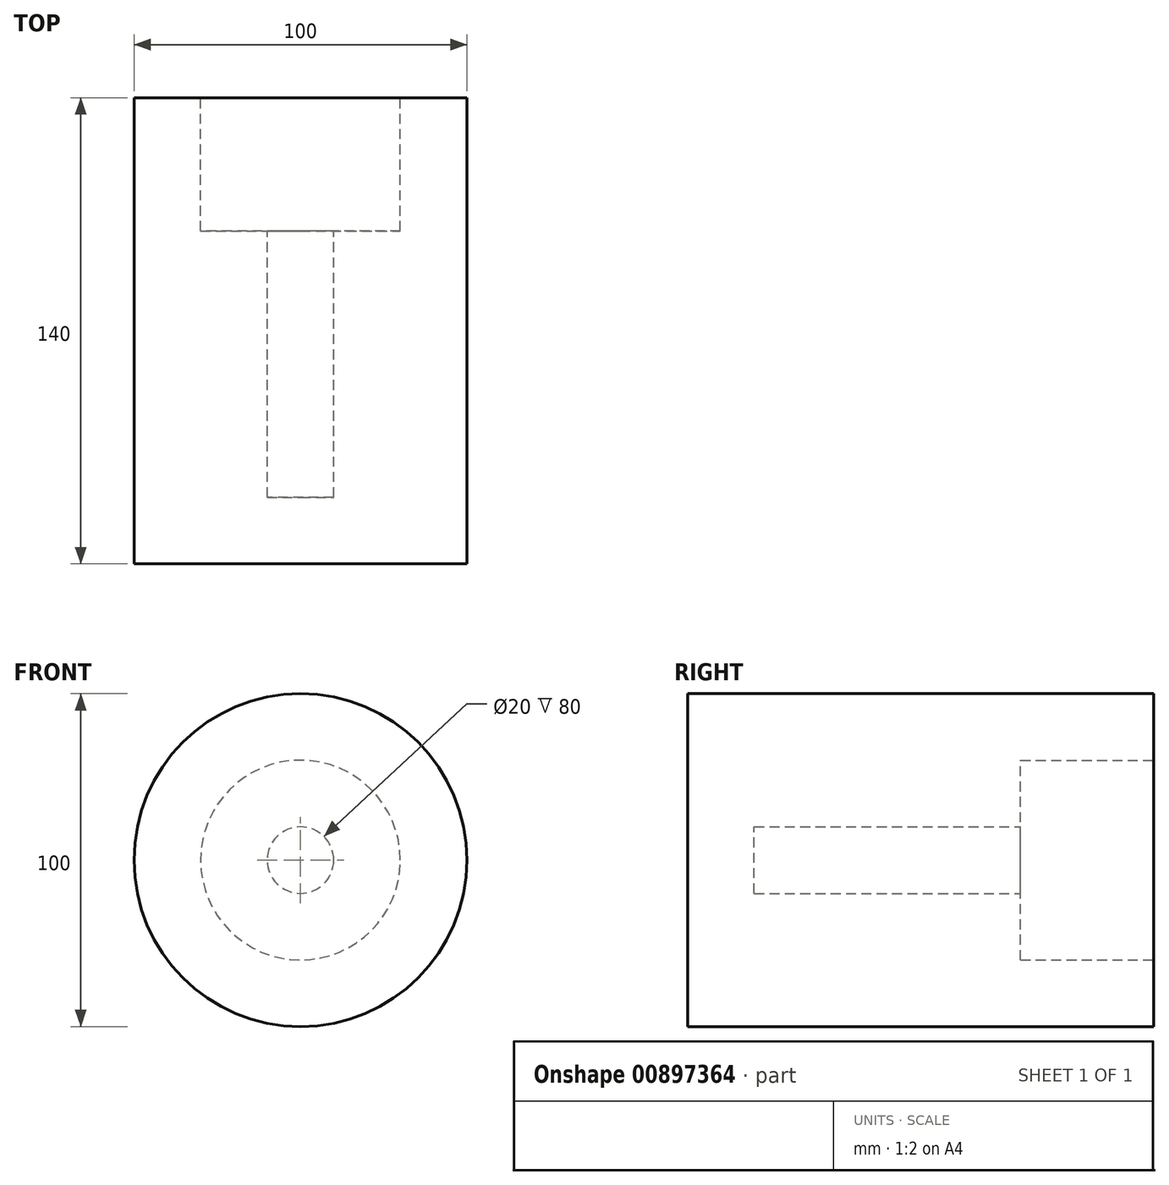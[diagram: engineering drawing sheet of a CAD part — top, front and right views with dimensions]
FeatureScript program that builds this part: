
annotation { "Feature Type Name" : "Feature", "Feature Type Description" : "" }
export const myFeature = defineFeature(function(context is Context, id is Id, definition is map)
    precondition{}
    {
        {
            var Q0;
            Q0=qCreatedBy(makeId("Front.planeOp"),FACE);
            var sketch = newSketch(context, id + "F0", { "sketchPlane" : qUnion([Q0])});
            skCircle(sketch, "E0", {"center": v(0, 0) * mm, "radius": 50 * mm});
            skSolve(sketch);
        }
        {
            var Q0;
            Q0=makeQuery(id+"F0.imprint","IMPRINT",FACE,{"disambiguationData":[TD([[makeQuery(id+"F0.imprint","IMPRINT",EDGE,{"derivedFrom":sQuery(id+"F0.wireOp",EDGE,"E0")}),1.0]])]});
            extrude(context, id + "F1", {"entities" : qUnion([Q0]), "depth" : 140 * mm, "offsetDistance" : 25.4 * mm});
        }
        {
            var Q0;
            Q0=qCreatedBy(makeId("Front.planeOp"),FACE);
            var sketch = newSketch(context, id + "F2", { "sketchPlane" : qUnion([Q0])});
            skCircle(sketch, "E1", {"center": v(0, 0) * mm, "radius": 30 * mm});
            skSolve(sketch);
        }
        {
            var Q0;
            Q0 = qSketchRegion(id + "F2", true);
            extrude(context, id + "F3", {"entities" : qUnion([Q0]), "operationType" : NewBodyOperationType.REMOVE, "depth" : 40 * mm, "offsetDistance" : 25.4 * mm});
        }
        {
            var Q0;
            Q0=qCreatedBy(makeId("Front.planeOp"),FACE);
            var sketch = newSketch(context, id + "F4", { "sketchPlane" : qUnion([Q0])});
            skCircle(sketch, "E2", {"center": v(0, 0) * mm, "radius": 10 * mm});
            skSolve(sketch);
        }
        {
            var Q0;
            Q0 = qSketchRegion(id + "F4", true);
            extrude(context, id + "F5", {"entities" : qUnion([Q0]), "operationType" : NewBodyOperationType.REMOVE, "depth" : 120 * mm, "offsetDistance" : 25.4 * mm});
        }
    });
